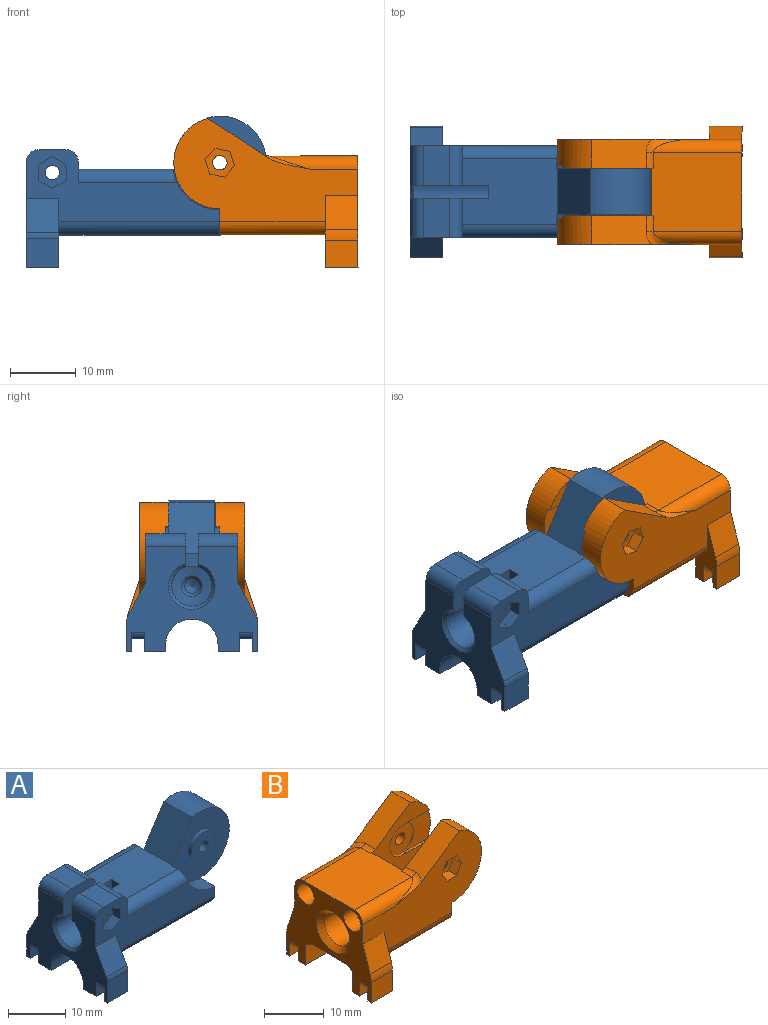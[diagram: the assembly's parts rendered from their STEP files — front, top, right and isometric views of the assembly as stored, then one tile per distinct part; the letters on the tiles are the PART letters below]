
ASSEMBLY  parts=2 mates=1
PART A: 82 faces, bbox 36.6x20x23.1 mm
  f0: plane 24.5x10mm, normal (0,0,-1), area 245mm2, adj f10,f56,f65,f68,f69
  f1: plane 6x4mm, normal (0,0,1), area 24mm2, adj f8,f41,f45,f46
  f2: plane 14.47x10mm, normal (0,0,1), area 136.4mm2, adj f3,f9,f13,f14,f16,f17,f39,f40
  f3: plane 6x3mm, normal (1,0,0), area 6.9mm2, adj f2,f7,f40,f43,f75
  f4: plane 20x16mm, normal (-1,0,0), area 180.7mm2, adj f7,f8,f40,f41,f42,f44,f46,f47
  f5: cylinder r=3.05mm len=18.9mm, axis (-1,0,0), area 338.8mm2, adj f39,f40,f41,f42,f77
  f6: cylinder r=1.1mm len=4mm, axis (0,-1,0), area 27.6mm2, adj f32,f40
  f7: plane 29.5x11mm, normal (0,1,0), area 162.7mm2, adj f3,f4,f9,f10,f11,f12,f15,f33
  f8: plane 29.5x11mm, normal (0,-1,0), area 162.7mm2, adj f1,f4,f10,f11,f12,f13,f14,f24
  f9: cylinder r=7.2mm len=7.13mm, axis (0,1,0), area 35.2mm2, adj f2,f7,f12,f17,f75
  f10: plane 14x3mm, normal (1,0,0), area 40.3mm2, adj f0,f7,f8,f11,f68,f69
  f11: plane 14x0.7mm, normal (1,0,-0.01), area 9.8mm2, adj f7,f8,f10,f12
  f12: plane 14x0.2mm, normal (1,0,0), area 2.1mm2, adj f7,f8,f9,f11,f13,f16,f17,f18
  f13: cylinder r=7.2mm len=7.13mm, axis (0,1,0), area 35.2mm2, adj f2,f8,f12,f16,f76
  f14: plane 6x3mm, normal (1,0,0), area 6.9mm2, adj f2,f8,f41,f45,f76
  f15: plane 6x4mm, normal (0,0,1), area 24mm2, adj f7,f40,f43,f44
  f16: plane 14.3x14.23mm, normal (0,-1,0), area 120.3mm2, adj f2,f12,f13,f18,f22,f70
  f17: plane 14.3x14.23mm, normal (0,1,0), area 120.3mm2, adj f2,f9,f12,f18,f21,f70
  f18: cylinder r=7.1mm len=14.2mm, axis (0,1,0), area 170.9mm2, adj f12,f16,f17,f70
  f19: cylinder r=1.1mm len=8.5mm, axis (0,1,0), area 58.7mm2, adj f20,f23
  f20: plane 6x6mm, normal (0,1,0), area 24.5mm2, adj f19,f21
  f21: cylinder r=3mm len=6mm, axis (0,1,0), area 14.1mm2, adj f17,f20
  f22: cylinder r=3mm len=6mm, axis (0,1,0), area 14.1mm2, adj f16,f23
  f23: plane 6x6mm, normal (0,-1,0), area 24.5mm2, adj f19,f22
  f24: plane 2.13x2mm, normal (-0.48,0,-0.88), area 4.8mm2, adj f8,f25,f29,f30
  f25: plane 2.07x2mm, normal (0.52,0,-0.85), area 4.8mm2, adj f8,f24,f26,f30
  f26: plane 2.42x2mm, normal (1,0,0.03), area 4.8mm2, adj f8,f25,f27,f30
  f27: plane 2.13x2mm, normal (0.48,0,0.88), area 4.8mm2, adj f8,f26,f28,f30
  f28: plane 2.07x2mm, normal (-0.52,0,0.85), area 4.8mm2, adj f8,f27,f29,f30
  f29: plane 2.42x2mm, normal (-1,0,-0.03), area 4.8mm2, adj f8,f24,f28,f30
  f30: plane 4.85x4.26mm, normal (0,-1,0), area 11.5mm2, adj f24,f25,f26,f27,f28,f29,f31
  f31: cylinder r=1.1mm len=4mm, axis (0,-1,0), area 27.6mm2, adj f30,f41
  f32: plane 4.78x4.55mm, normal (0,1,0), area 11.5mm2, adj f6,f33,f34,f35,f36,f37,f38
  f33: plane 2.27x2mm, normal (0.35,0,-0.94), area 4.8mm2, adj f7,f32,f34,f38
  f34: plane 2x1.87mm, normal (-0.64,0,-0.77), area 4.8mm2, adj f7,f32,f33,f35
  f35: plane 2.39x2mm, normal (-0.99,0,0.17), area 4.8mm2, adj f7,f32,f34,f36
  f36: plane 2.27x2mm, normal (-0.35,0,0.94), area 4.8mm2, adj f7,f32,f35,f37
  f37: plane 2x1.87mm, normal (0.64,0,0.77), area 4.8mm2, adj f7,f32,f36,f38
  f38: plane 2.39x2mm, normal (0.99,0,-0.17), area 4.8mm2, adj f7,f32,f33,f37
  f39: plane 2.12x2mm, normal (-1,0,0), area 4mm2, adj f2,f5,f40,f41
  f40: plane 12.01x5.13mm, normal (0,-1,0), area 43.8mm2, adj f2,f3,f4,f5,f6,f15,f39,f42
  f41: plane 12.01x5.13mm, normal (0,1,0), area 43.8mm2, adj f1,f2,f4,f5,f14,f31,f39,f42
  f42: cone r=3.05mm half-angle=45deg, axis (-1,0,0), area 13.2mm2, adj f4,f5,f40,f41
  f43: cylinder r=2mm len=6mm, axis (0,1,0), area 18.8mm2, adj f3,f7,f15,f40
  f44: cylinder r=2mm len=6mm, axis (0,-1,0), area 18.8mm2, adj f4,f7,f15,f40
  f45: cylinder r=2mm len=6mm, axis (0,1,0), area 18.8mm2, adj f1,f8,f14,f41
  f46: cylinder r=2mm len=6mm, axis (0,-1,0), area 18.8mm2, adj f1,f4,f8,f41
  f47: plane 5.05x5mm, normal (0,0.88,0.48), area 28.8mm2, adj f4,f7,f56,f66
  f48: plane 5x4.49mm, normal (0,1,0), area 22.5mm2, adj f4,f49,f56,f66
  f49: plane 5x0.8mm, normal (0,0,-1), area 4mm2, adj f4,f48,f50,f56
  f50: plane 5x3mm, normal (0,-1,0), area 10.4mm2, adj f4,f49,f51,f56,f71,f72
  f51: plane 3x2mm, normal (0,0,-1), area 6mm2, adj f50,f52,f71,f72
  f52: plane 5x3mm, normal (0,1,0), area 10.4mm2, adj f4,f51,f53,f56,f71,f72
  f53: plane 5x3.2mm, normal (0,0,-1), area 16mm2, adj f4,f52,f54,f56
  f54: plane 5x1mm, normal (0,-1,0), area 5mm2, adj f4,f53,f55,f56
  f55: cylinder r=4mm len=8mm, axis (-1,0,0), area 62.8mm2, adj f4,f54,f56,f59,f65
  f56: plane 10.5x10mm, normal (1,0,0), area 36.5mm2, adj f0,f7,f47,f48,f49,f50,f52,f53
  f57: plane 5x4.49mm, normal (0,-1,0), area 22.5mm2, adj f4,f64,f65,f67
  f58: plane 5.05x5mm, normal (0,-0.88,0.48), area 28.8mm2, adj f4,f8,f65,f67
  f59: plane 5x1mm, normal (0,1,0), area 5mm2, adj f4,f55,f60,f65
  f60: plane 5x3.2mm, normal (0,0,-1), area 16mm2, adj f4,f59,f61,f65
  f61: plane 5x3mm, normal (0,-1,0), area 10.4mm2, adj f4,f60,f62,f65,f73,f74
  f62: plane 3x2mm, normal (0,0,-1), area 6mm2, adj f61,f63,f73,f74
  f63: plane 5x3mm, normal (0,1,0), area 10.4mm2, adj f4,f62,f64,f65,f73,f74
  f64: plane 5x0.8mm, normal (0,0,-1), area 4mm2, adj f4,f57,f63,f65
  f65: plane 10.5x10mm, normal (1,0,0), area 36.5mm2, adj f0,f8,f55,f57,f58,f59,f60,f61
  f66: cylinder r=2mm len=5mm, axis (1,0,0), area 5mm2, adj f4,f47,f48,f56
  f67: cylinder r=2mm len=5mm, axis (1,0,0), area 5mm2, adj f4,f57,f58,f65
  f68: cylinder r=2mm len=24.5mm, axis (1,0,0), area 77mm2, adj f0,f7,f10,f56
  f69: cylinder r=2mm len=24.5mm, axis (-1,0,0), area 77mm2, adj f0,f8,f10,f65
  f70: plane 7.79x7mm, normal (-0.84,0,0.54), area 64.6mm2, adj f2,f16,f17,f18
  f71: cylinder r=1mm len=2mm, axis (0,-1,0), area 3.1mm2, adj f4,f50,f51,f52
  f72: cylinder r=1mm len=2mm, axis (0,1,0), area 3.1mm2, adj f50,f51,f52,f56
  f73: cylinder r=1mm len=2mm, axis (0,-1,0), area 3.1mm2, adj f4,f61,f62,f63
  f74: cylinder r=1mm len=2mm, axis (0,1,0), area 3.1mm2, adj f61,f62,f63,f65
  f75: cylinder r=2mm len=14.95mm, axis (-1,0,0), area 45.7mm2, adj f2,f3,f7,f9
  f76: cylinder r=2mm len=14.95mm, axis (1,0,0), area 45.7mm2, adj f2,f8,f13,f14
  f77: cone r=0.05mm half-angle=78.7deg, axis (-1,0,0), area 21.7mm2, adj f5,f81
  f78: cylinder r=1.1mm len=7.21mm, axis (-1,0,0), area 49.8mm2, adj f80,f81
  f79: plane 0.2x0.2mm, normal (-1,0,0), area 0mm2, adj f80
  f80: cone r=0.1mm half-angle=63.4deg, axis (-1,0,0), area 4.2mm2, adj f78,f79
  f81: cone r=1.59mm half-angle=39.3deg, axis (-1,0,0), area 6.5mm2, adj f77,f78
PART B: 92 faces, bbox 28x20x22.8 mm
  f0: plane 7.2x1mm, normal (1,0,0), area 7.2mm2, adj f12,f13,f18,f87
  f1: plane 5x4mm, normal (0,-1,0), area 20mm2, adj f14,f51,f52,f66
  f2: plane 21x12mm, normal (0,0,-1), area 227mm2, adj f14,f15,f52,f60,f63,f64,f65,f66
  f3: plane 5x4mm, normal (0,1,0), area 20mm2, adj f14,f55,f60,f65
  f4: plane 28x15.76mm, normal (0,1,0), area 244.5mm2, adj f10,f14,f15,f36,f37,f38,f39,f40
  f5: cylinder r=1.1mm len=2.2mm, axis (0,-1,0), area 12.4mm2, adj f16,f42
  f6: plane 28x15.76mm, normal (0,-1,0), area 244.5mm2, adj f8,f14,f15,f29,f30,f31,f32,f33
  f7: cylinder r=1.1mm len=2.2mm, axis (0,-1,0), area 12.4mm2, adj f17,f35
  f8: cylinder r=7mm len=13.76mm, axis (0,1,0), area 85.4mm2, adj f6,f12,f15,f24,f25,f26,f62
  f9: cylinder r=3.05mm len=6.1mm, axis (0,-1,0), area 7.5mm2, adj f12,f17,f24,f27,f28
  f10: cylinder r=7mm len=13.76mm, axis (0,1,0), area 85.4mm2, adj f4,f15,f18,f19,f20,f21,f61
  f11: cylinder r=3.05mm len=6.1mm, axis (0,-1,0), area 7.5mm2, adj f16,f18,f19,f22,f23
  f12: plane 13.8x13.76mm, normal (0,1,0), area 82.5mm2, adj f0,f8,f9,f13,f25,f26,f27,f28
  f13: plane 13.75x12mm, normal (0,0,1), area 163.7mm2, adj f0,f12,f14,f18,f71,f72,f73,f75
  f14: plane 20x17mm, normal (-1,0,0), area 161mm2, adj f1,f2,f3,f4,f6,f13,f44,f45
  f15: plane 16x4mm, normal (1,0,0), area 62.3mm2, adj f2,f4,f6,f8,f10,f63,f64,f80
  f16: plane 6.1x6.1mm, normal (0,-1,0), area 25.4mm2, adj f5,f11
  f17: plane 6.1x6.1mm, normal (0,1,0), area 25.4mm2, adj f7,f9
  f18: plane 13.8x13.76mm, normal (0,-1,0), area 82.5mm2, adj f0,f10,f11,f13,f20,f21,f22,f23
  f19: plane 6.25x6.2mm, normal (0,-1,0), area 27.2mm2, adj f10,f11,f20,f21,f22,f23
  f20: plane 5.53x0.5mm, normal (0,0,1), area 2.8mm2, adj f10,f18,f19,f23
  f21: plane 5.53x0.5mm, normal (0,0,-1), area 2.8mm2, adj f10,f18,f19,f22
  f22: plane 0.5x0.14mm, normal (1,0,0), area 0.1mm2, adj f11,f18,f19,f21
  f23: plane 0.5x0.14mm, normal (1,0,0), area 0.1mm2, adj f11,f18,f19,f20
  f24: plane 6.25x6.2mm, normal (0,1,0), area 27.2mm2, adj f8,f9,f25,f26,f27,f28
  f25: plane 5.53x0.5mm, normal (0,0,-1), area 2.8mm2, adj f8,f12,f24,f27
  f26: plane 5.53x0.5mm, normal (0,0,1), area 2.8mm2, adj f8,f12,f24,f28
  f27: plane 0.5x0.14mm, normal (1,0,0), area 0.1mm2, adj f9,f12,f24,f25
  f28: plane 0.5x0.14mm, normal (1,0,0), area 0.1mm2, adj f9,f12,f24,f26
  f29: plane 2.31x2mm, normal (0,0,-1), area 4.6mm2, adj f6,f30,f34,f35
  f30: plane 2x2mm, normal (0.87,0,-0.5), area 4.6mm2, adj f6,f29,f31,f35
  f31: plane 2x2mm, normal (0.87,0,0.5), area 4.6mm2, adj f6,f30,f32,f35
  f32: plane 2.31x2mm, normal (0,0,1), area 4.6mm2, adj f6,f31,f33,f35
  f33: plane 2x2mm, normal (-0.87,0,0.5), area 4.6mm2, adj f6,f32,f34,f35
  f34: plane 2x2mm, normal (-0.87,0,-0.5), area 4.6mm2, adj f6,f29,f33,f35
  f35: plane 4.62x4mm, normal (0,-1,0), area 10.1mm2, adj f7,f29,f30,f31,f32,f33,f34
  f36: plane 2.26x2mm, normal (0.2,0,-0.98), area 4.6mm2, adj f4,f37,f41,f42
  f37: plane 2x1.73mm, normal (-0.75,0,-0.66), area 4.6mm2, adj f4,f36,f38,f42
  f38: plane 2.19x2mm, normal (-0.95,0,0.32), area 4.6mm2, adj f4,f37,f39,f42
  f39: plane 2.26x2mm, normal (-0.2,0,0.98), area 4.6mm2, adj f4,f38,f40,f42
  f40: plane 2x1.73mm, normal (0.75,0,0.66), area 4.6mm2, adj f4,f39,f41,f42
  f41: plane 2.19x2mm, normal (0.95,0,-0.32), area 4.6mm2, adj f4,f36,f40,f42
  f42: plane 4.53x4.38mm, normal (0,1,0), area 10.1mm2, adj f5,f36,f37,f38,f39,f40,f41
  f43: cylinder r=3mm len=10mm, axis (-1,0,0), area 188.5mm2, adj f44,f79
  f44: cone r=3mm half-angle=45deg, axis (-1,0,0), area 31.1mm2, adj f14,f43
  f45: plane 5.23x5mm, normal (0,0.95,0.32), area 27.6mm2, adj f4,f14,f52,f78
  f46: plane 5x4.19mm, normal (0,1,0), area 20.9mm2, adj f14,f47,f52,f78
  f47: plane 5x0.8mm, normal (0,0,-1), area 4mm2, adj f14,f46,f48,f52
  f48: plane 5x3mm, normal (0,-1,0), area 10.4mm2, adj f14,f47,f49,f52,f69,f70
  f49: plane 3x2mm, normal (0,0,-1), area 6mm2, adj f48,f50,f69,f70
  f50: plane 5x3mm, normal (0,1,0), area 10.4mm2, adj f14,f49,f51,f52,f69,f70
  f51: plane 5x1.7mm, normal (0,0,-1), area 8.5mm2, adj f1,f14,f50,f52
  f52: plane 11x6.5mm, normal (1,0,0), area 23.9mm2, adj f1,f2,f4,f45,f46,f47,f48,f50
  f53: plane 5x4.19mm, normal (0,-1,0), area 20.9mm2, adj f14,f59,f60,f77
  f54: plane 5.23x5mm, normal (0,-0.95,0.32), area 27.6mm2, adj f6,f14,f60,f77
  f55: plane 5x1.7mm, normal (0,0,-1), area 8.5mm2, adj f3,f14,f56,f60
  f56: plane 5x3mm, normal (0,-1,0), area 10.4mm2, adj f14,f55,f57,f60,f67,f68
  f57: plane 3x2mm, normal (0,0,-1), area 6mm2, adj f56,f58,f67,f68
  f58: plane 5x3mm, normal (0,1,0), area 10.4mm2, adj f14,f57,f59,f60,f67,f68
  f59: plane 5x0.8mm, normal (0,0,-1), area 4mm2, adj f14,f53,f58,f60
  f60: plane 11x6.5mm, normal (1,0,0), area 23.9mm2, adj f2,f3,f6,f53,f54,f55,f56,f58
  f61: plane 9.06x5.97mm, normal (-0.55,0,0.84), area 44.1mm2, adj f4,f10,f18,f75,f76
  f62: plane 9.06x5.97mm, normal (-0.55,0,0.84), area 44.1mm2, adj f6,f8,f12,f73,f74
  f63: cylinder r=2mm len=16mm, axis (1,0,0), area 50.3mm2, adj f2,f4,f15,f52
  f64: cylinder r=2mm len=16mm, axis (-1,0,0), area 50.3mm2, adj f2,f6,f15,f60
  f65: cylinder r=2.5mm len=5mm, axis (-1,0,0), area 11.6mm2, adj f2,f3,f14,f60
  f66: cylinder r=2.5mm len=5mm, axis (-1,0,0), area 11.6mm2, adj f1,f2,f14,f52
  f67: cylinder r=1mm len=2mm, axis (0,1,0), area 3.1mm2, adj f14,f56,f57,f58
  f68: cylinder r=1mm len=2mm, axis (0,1,0), area 3.1mm2, adj f56,f57,f58,f60
  f69: cylinder r=1mm len=2mm, axis (0,1,0), area 3.1mm2, adj f14,f48,f49,f50
  f70: cylinder r=1mm len=2mm, axis (0,1,0), area 3.1mm2, adj f48,f49,f50,f52
  f71: cylinder r=2mm len=13.47mm, axis (-1,0,0), area 32.8mm2, adj f4,f13,f14,f76
  f72: cylinder r=2mm len=13.47mm, axis (1,0,0), area 32.8mm2, adj f6,f13,f14,f74
  f73: cylinder r=2mm len=2.4mm, axis (0,-1,0), area 2.8mm2, adj f12,f13,f62,f74
  f74: bspline ~7.18x4mm, area 5.4mm2, adj f6,f62,f72,f73
  f75: cylinder r=2mm len=2.4mm, axis (0,-1,0), area 2.8mm2, adj f13,f18,f61,f76
  f76: bspline ~7.18x4mm, area 5.4mm2, adj f4,f61,f71,f75
  f77: cylinder r=5mm len=5mm, axis (1,0,0), area 8mm2, adj f14,f53,f54,f60
  f78: cylinder r=5mm len=5mm, axis (1,0,0), area 8mm2, adj f14,f45,f46,f52
  f79: cone r=3mm half-angle=71.6deg, axis (-1,0,0), area 29.8mm2, adj f43
  f80: plane 7.2x0.25mm, normal (0,0,1), area 1.8mm2, adj f12,f15,f18,f87
  f81: cylinder r=2mm len=4mm, axis (-1,0,0), area 44mm2, adj f14,f91
  f82: cylinder r=2mm len=4mm, axis (-1,0,0), area 44mm2, adj f14,f90
  f83: plane 0.1x0.1mm, normal (-1,0,0), area 0mm2, adj f88
  f84: cylinder r=1.05mm len=13.53mm, axis (-1,0,0), area 89.2mm2, adj f88,f91
  f85: plane 0.1x0.1mm, normal (-1,0,0), area 0mm2, adj f89
  f86: cylinder r=1.05mm len=13.53mm, axis (-1,0,0), area 89.2mm2, adj f89,f90
  f87: cylinder r=7mm len=7.2mm, axis (0,1,0), area 79.2mm2, adj f0,f12,f18,f80
  f88: cone r=0.05mm half-angle=63.4deg, axis (-1,0,0), area 3.9mm2, adj f83,f84
  f89: cone r=0.05mm half-angle=63.4deg, axis (-1,0,0), area 3.9mm2, adj f85,f86
  f90: cone r=1mm half-angle=63.4deg, axis (-1,0,0), area 10.2mm2, adj f82,f86
  f91: cone r=1mm half-angle=63.4deg, axis (-1,0,0), area 10.2mm2, adj f81,f84
PLACE A t=(-6.58,-2.35,2.17)mm fixed
PLACE B rot(axis=(0,0,-1),180deg) t=(5.68,-2.4,2.69)mm
MATE revolute A.f9 <-> B.f5  axis (0,-1,0) through (0.42,-6.6,6.17)mm
